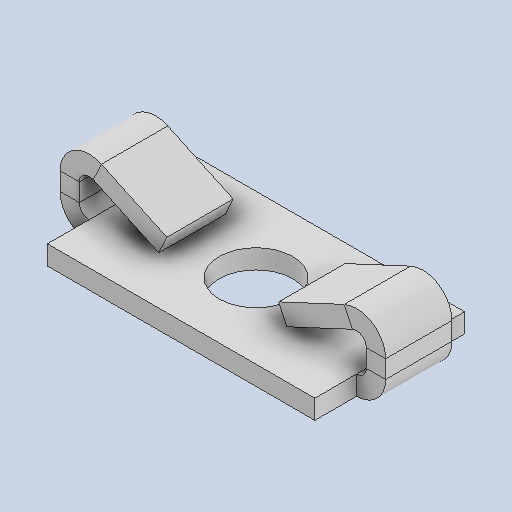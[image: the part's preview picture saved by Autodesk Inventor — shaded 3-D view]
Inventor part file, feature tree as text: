
AUTODESK INVENTOR PART (.ipt)
format: ipt  version: 2022 (Build 260153000, 153)  size: 126,976 bytes
history: native  units: in
note: dims shown in document units (in); Inventor stores cm internally (conversion verified against a paired STEP export)
features: mirror x1
ambient origin geometry x8: Origin, YZ Plane, XZ Plane, XY Plane, X Axis, Y Axis, Z Axis, Center Point
bodies: Solid1 (feature_tree)
feature tree (1):
  mirror  "Mirror1"
